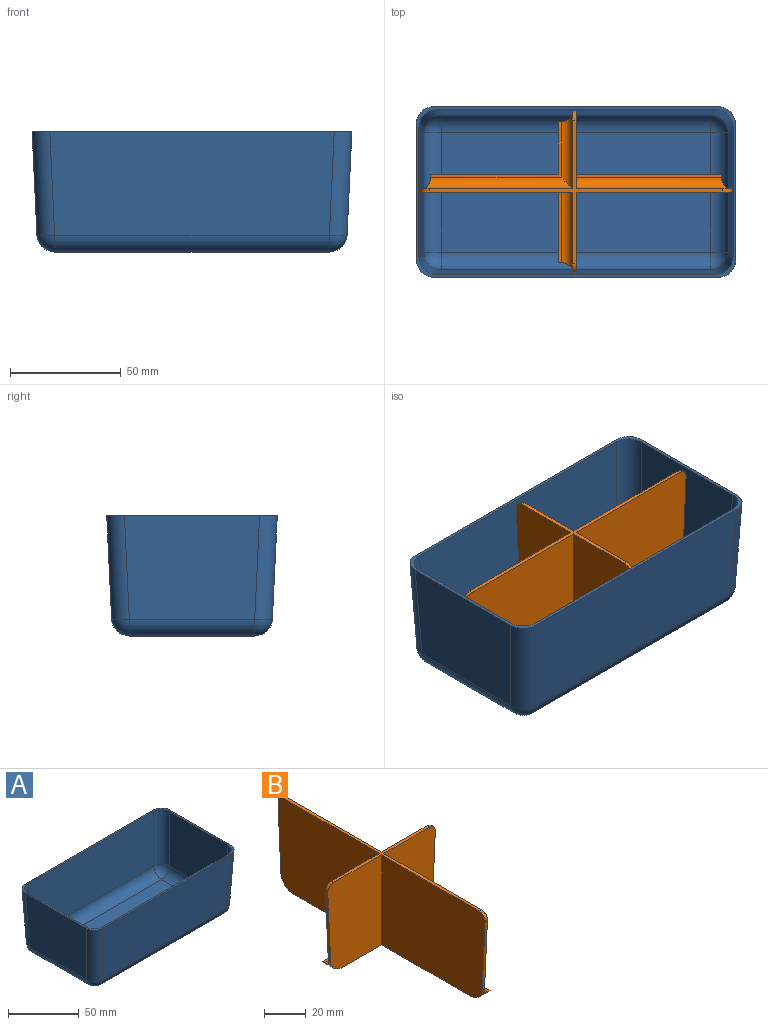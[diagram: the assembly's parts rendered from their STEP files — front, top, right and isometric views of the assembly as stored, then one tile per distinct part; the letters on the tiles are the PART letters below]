
ASSEMBLY  parts=2 mates=1
PART A: 35 faces, bbox 144.6x77.1x54.5 mm
  f0: plane 61.12x46.68mm, normal (1,0,-0.05), area 2753.1mm2, adj f8,f13,f16,f26
  f1: plane 128.62x46.68mm, normal (0,1,-0.05), area 5907.3mm2, adj f8,f13,f14,f22
  f2: plane 61.12x46.68mm, normal (-1,0,-0.05), area 2753.1mm2, adj f8,f14,f15,f19
  f3: plane 58.52x45.38mm, normal (1,0,0.05), area 2561.1mm2, adj f8,f9,f12,f32
  f4: plane 126.02x45.38mm, normal (0,-1,0.05), area 5627.4mm2, adj f8,f9,f10,f28
  f5: plane 58.52x45.38mm, normal (-1,0,0.05), area 2561.1mm2, adj f8,f10,f11,f29
  f6: plane 126.02x45.38mm, normal (0,1,0.05), area 5627.4mm2, adj f8,f11,f12,f33
  f7: plane 128.62x46.68mm, normal (0,-1,-0.05), area 5907.3mm2, adj f8,f15,f16,f23
  f8: plane 144.6x77.1mm, normal (0,0,1), area 569.7mm2, adj f0,f1,f2,f3,f4,f5,f6,f7
  f9: cylinder r=8mm len=45.69mm, axis (0.05,-0.05,-1), area 572mm2, adj f3,f4,f8,f30
  f10: cylinder r=8mm len=45.69mm, axis (-0.05,-0.05,-1), area 572mm2, adj f4,f5,f8,f27
  f11: cylinder r=8mm len=45.69mm, axis (-0.05,0.05,-1), area 572mm2, adj f5,f6,f8,f31
  f12: cylinder r=8mm len=45.69mm, axis (0.05,0.05,-1), area 572mm2, adj f3,f6,f8,f34
  f13: cylinder r=8mm len=46.99mm, axis (0.05,0.05,1), area 588.3mm2, adj f0,f1,f8,f24
  f14: cylinder r=8mm len=46.99mm, axis (-0.05,0.05,1), area 588.3mm2, adj f1,f2,f8,f20
  f15: cylinder r=8mm len=46.99mm, axis (-0.05,-0.05,1), area 588.3mm2, adj f2,f7,f8,f21
  f16: cylinder r=8mm len=46.99mm, axis (0.05,-0.05,1), area 588.3mm2, adj f0,f7,f8,f25
  f17: plane 121.74x54.24mm, normal (0,0,1), area 6602.8mm2, adj f28,f29,f32,f33
  f18: plane 124.22x56.72mm, normal (0,0,-1), area 7044.9mm2, adj f19,f22,f23,f26
  f19: cylinder r=8mm len=56.72mm, axis (0,1,0), area 691.3mm2, adj f2,f18,f20,f21
  f20: sphere r=8mm, area 94.5mm2, adj f14,f19,f22
  f21: sphere r=8mm, area 94.5mm2, adj f15,f19,f23
  f22: cylinder r=8mm len=124.22mm, axis (1,0,0), area 1514.1mm2, adj f1,f18,f20,f24
  f23: cylinder r=8mm len=124.22mm, axis (1,0,0), area 1514.1mm2, adj f7,f18,f21,f25
  f24: sphere r=8mm, area 94.5mm2, adj f13,f22,f26
  f25: sphere r=8mm, area 94.5mm2, adj f16,f23,f26
  f26: cylinder r=8mm len=56.72mm, axis (0,-1,0), area 691.3mm2, adj f0,f18,f24,f25
  f27: sphere r=8mm, area 94.5mm2, adj f10,f28,f29
  f28: cylinder r=8mm len=121.74mm, axis (-1,0,0), area 1483.9mm2, adj f4,f17,f27,f30
  f29: cylinder r=8mm len=54.24mm, axis (0,-1,0), area 661.1mm2, adj f5,f17,f27,f31
  f30: sphere r=8mm, area 94.5mm2, adj f9,f28,f32
  f31: sphere r=8mm, area 94.5mm2, adj f11,f29,f33
  f32: cylinder r=8mm len=54.24mm, axis (0,-1,0), area 661.1mm2, adj f3,f17,f30,f34
  f33: cylinder r=8mm len=121.74mm, axis (-1,0,0), area 1483.9mm2, adj f6,f17,f31,f34
  f34: sphere r=8mm, area 94.5mm2, adj f12,f32,f33
PART B: 33 faces, bbox 73.1x140.8x53 mm
  f0: plane 57.76x2mm, normal (1,0,0), area 112.2mm2, adj f7,f8,f17,f23
  f1: plane 65.76x2mm, normal (1,0,0), area 128.2mm2, adj f2,f7,f19,f24
  f2: plane 65.76x1.4mm, normal (0,0,1), area 92.1mm2, adj f1,f19,f24,f25
  f3: plane 68.81x46mm, normal (1,0,0), area 3120.3mm2, adj f9,f11,f18,f23,f26,f31
  f4: plane 70.41x46mm, normal (1,0,0), area 3193.9mm2, adj f9,f10,f19,f24,f25,f32
  f5: plane 68.81x53mm, normal (-1,0,0), area 3556.5mm2, adj f7,f9,f11,f13,f14,f15,f23,f28
  f6: plane 70.41x53mm, normal (-1,0,0), area 3659.4mm2, adj f7,f9,f10,f16,f24,f32
  f7: plane 120.94x53.24mm, normal (0,0,-1), area 1329.4mm2, adj f0,f1,f5,f6,f15,f16,f17,f19
  f8: plane 59.16x25.31mm, normal (0,0,1), area 116.3mm2, adj f0,f17,f22,f23,f26,f27
  f9: plane 132.81x65.11mm, normal (0,0,1), area 314.1mm2, adj f3,f4,f5,f6,f13,f16,f18,f19
  f10: plane 41.19x1.94mm, normal (0,-1,-0.05), area 66mm2, adj f4,f6,f24,f32
  f11: plane 41.19x1.94mm, normal (0,1,-0.05), area 66mm2, adj f3,f5,f23,f31
  f12: plane 41.19x1.94mm, normal (-1,0,-0.05), area 66mm2, adj f13,f16,f21,f29
  f13: plane 46x36.56mm, normal (0,1,0), area 1636.8mm2, adj f5,f9,f12,f21,f28,f29
  f14: plane 31.91x1.4mm, normal (0,0,1), area 44.7mm2, adj f5,f15,f21,f28
  f15: plane 31.91x2mm, normal (0,1,0), area 60.5mm2, adj f5,f7,f14,f21
  f16: plane 53x36.56mm, normal (0,-1,0), area 1865.4mm2, adj f6,f7,f9,f12,f21,f29
  f17: plane 23.91x2mm, normal (0,1,0), area 44.5mm2, adj f0,f7,f8,f22
  f18: plane 46x34.96mm, normal (0,1,0), area 1563.2mm2, adj f3,f9,f20,f22,f27,f30
  f19: plane 53x34.96mm, normal (0,-1,0), area 1762.4mm2, adj f1,f2,f4,f7,f9,f20,f22,f25
  f20: plane 41.19x1.94mm, normal (1,0,-0.05), area 66mm2, adj f18,f19,f22,f30
  f21: cylinder r=8mm len=8mm, axis (0,1,0), area 63.5mm2, adj f7,f12,f13,f14,f15,f16,f28
  f22: cylinder r=8mm len=8mm, axis (0,1,0), area 63.5mm2, adj f7,f8,f17,f18,f19,f20,f27
  f23: cylinder r=8mm len=8mm, axis (1,0,0), area 63.5mm2, adj f0,f3,f5,f7,f8,f11,f26
  f24: cylinder r=8mm len=8mm, axis (1,0,0), area 63.5mm2, adj f1,f2,f4,f6,f7,f10,f25
  f25: cylinder r=5mm len=68.41mm, axis (0,1,0), area 526.6mm2, adj f2,f4,f19,f24
  f26: cylinder r=5mm len=66.81mm, axis (0,1,0), area 499.8mm2, adj f3,f8,f23,f27
  f27: cylinder r=5mm len=32.96mm, axis (-1,0,0), area 233.9mm2, adj f8,f18,f22,f26
  f28: cylinder r=5mm len=34.56mm, axis (-1,0,0), area 260.8mm2, adj f5,f13,f14,f21
  f29: cylinder r=4mm len=4.19mm, axis (0,-1,0), area 10.4mm2, adj f9,f12,f13,f16
  f30: cylinder r=4mm len=4.19mm, axis (0,-1,0), area 10.4mm2, adj f9,f18,f19,f20
  f31: cylinder r=4mm len=4.19mm, axis (-1,0,0), area 10.4mm2, adj f3,f5,f9,f11
  f32: cylinder r=4mm len=4.19mm, axis (-1,0,0), area 10.4mm2, adj f4,f6,f9,f10
PLACE A t=(-25.77,-0.08,-3.66)mm
PLACE B rot(axis=(0,0,1),90deg) t=(-25.77,-0.08,-3.66)mm
MATE revolute B.f7 <-> A.f17  axis (0,0,1) through (-25.77,-0.08,-3.66)mm
